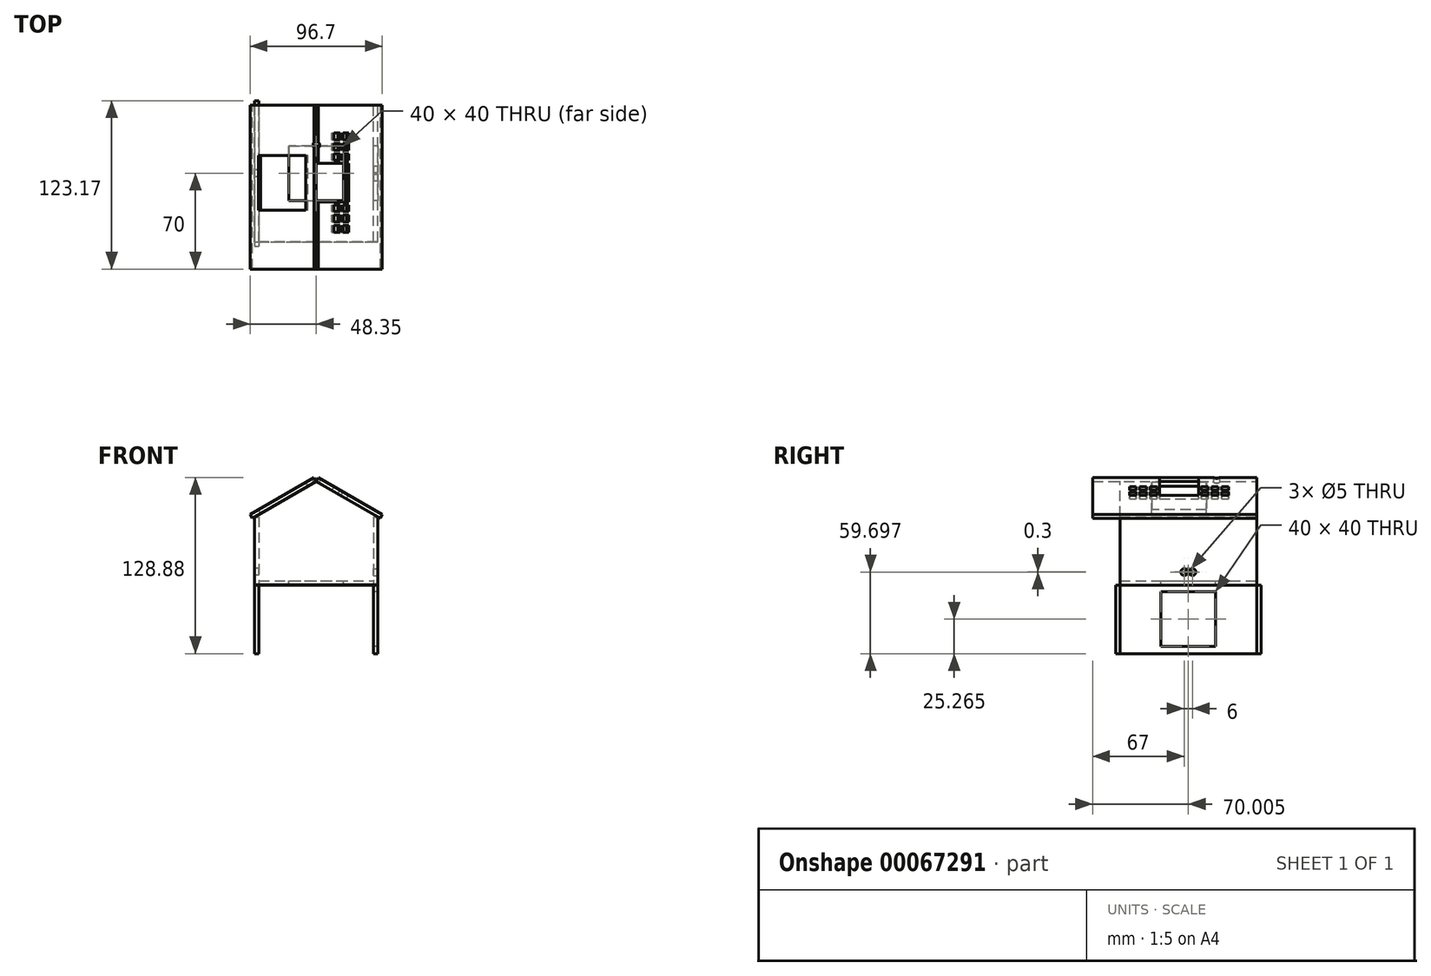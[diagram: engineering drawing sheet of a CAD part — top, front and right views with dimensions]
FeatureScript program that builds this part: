
annotation { "Feature Type Name" : "Feature", "Feature Type Description" : "" }
export const myFeature = defineFeature(function(context is Context, id is Id, definition is map)
    precondition{}
    {
        {
            var Q0;
            Q0=qCreatedBy(makeId("Front.planeOp"),FACE);
            var sketch = newSketch(context, id + "F0", { "sketchPlane" : qUnion([Q0])});
            skLineSegment(sketch, "E0.rect.bottom", {"start": v(-45, -25) * mm, "end": v(45, -25) * mm});
            skLineSegment(sketch, "E0.rect.top", {"start": v(-45, 25) * mm, "end": v(45, 25) * mm});
            skLineSegment(sketch, "E0.rect.left", {"start": v(-45, -25) * mm, "end": v(-45, 25) * mm});
            skLineSegment(sketch, "E0.rect.right", {"start": v(45, -25) * mm, "end": v(45, 25) * mm});
            skPoint(sketch, "E0.rect.middle", {"position": v(0, 0) * mm});
            skLineSegment(sketch, "E1", {"start": v(0, 25) * mm, "end": v(0, 50.98) * mm});
            skPoint(sketch, "E1.endSnap0", {"position": v(0, 25) * mm});
            skLineSegment(sketch, "E2", {"start": v(45, 25) * mm, "end": v(0, 50.98) * mm});
            skLineSegment(sketch, "E3", {"start": v(0, 50.98) * mm, "end": v(-45, 25) * mm});
            skSolve(sketch);
        }
        {
            var Q0;
            Q0 = qSketchRegion(id + "F0", true);
            extrude(context, id + "F1", {"entities" : qUnion([Q0]), "oppositeDirection" : true, "depth" : 1 / 203.2 * mm});
        }
        {
            var Q0;
            Q0=qCreatedBy(makeId("Front.planeOp"),FACE);
            var sketch = newSketch(context, id + "F2", { "sketchPlane" : qUnion([Q0])});
            skLineSegment(sketch, "E4.bottom", {"start": v(41.87, 24.95) * mm, "end": v(45.04, 24.95) * mm});
            skLineSegment(sketch, "E4.top", {"start": v(41.87, -25.05) * mm, "end": v(45.04, -25.05) * mm});
            skLineSegment(sketch, "E4.left", {"start": v(41.87, 24.95) * mm, "end": v(41.87, -25.05) * mm});
            skLineSegment(sketch, "E4.right", {"start": v(45.04, 24.95) * mm, "end": v(45.04, -25.05) * mm});
            skSolve(sketch);
        }
        {
            var Q0;
            Q0 = qSketchRegion(id + "F2", true);
            extrude(context, id + "F3", {"entities" : qUnion([Q0]), "depth" : 100 * mm});
        }
        {
            var Q0;
            Q0=qCreatedBy(makeId("Front.planeOp"),FACE);
            var sketch = newSketch(context, id + "F4", { "sketchPlane" : qUnion([Q0])});
            skLineSegment(sketch, "E5.bottom", {"start": v(-45, 25) * mm, "end": v(-41.83, 25) * mm});
            skLineSegment(sketch, "E5.top", {"start": v(-45, -25) * mm, "end": v(-41.83, -25) * mm});
            skLineSegment(sketch, "E5.left", {"start": v(-45, 25) * mm, "end": v(-45, -25) * mm});
            skLineSegment(sketch, "E5.right", {"start": v(-41.83, 25) * mm, "end": v(-41.83, -25) * mm});
            skSolve(sketch);
        }
        {
            var Q0;
            Q0 = qSketchRegion(id + "F4", true);
            extrude(context, id + "F5", {"entities" : qUnion([Q0]), "depth" : 100 * mm});
        }
        {
            var Q0;
            Q0=makeQuery(id+"F5.opExtrude","CAP_FACE",FACE,{"disambiguationData":[OSD([sQuery(id+"F4.wireOp",EDGE,"E5.bottom"),sQuery(id+"F4.wireOp",EDGE,"E5.top"),sQuery(id+"F4.wireOp",EDGE,"E5.left"),sQuery(id+"F4.wireOp",EDGE,"E5.right")])],"isStart":false});
            var sketch = newSketch(context, id + "F6", { "sketchPlane" : qUnion([Q0])});
            skLineSegment(sketch, "E6.rect.top", {"start": v(-45, 25.24) * mm, "end": v(45, 25.24) * mm});
            skLineSegment(sketch, "E6.rect.bottom", {"start": v(-45, -24.76) * mm, "end": v(45, -24.76) * mm});
            skLineSegment(sketch, "E6.rect.left", {"start": v(-45, -24.76) * mm, "end": v(-45, 25.24) * mm});
            skLineSegment(sketch, "E6.rect.right", {"start": v(45, -24.76) * mm, "end": v(45, 25.24) * mm});
            skLineSegment(sketch, "E7", {"start": v(0, 25.24) * mm, "end": v(0, 51.22) * mm});
            skLineSegment(sketch, "E8", {"start": v(45, 25.24) * mm, "end": v(0, 51.22) * mm});
            skLineSegment(sketch, "E9", {"start": v(0, 51.22) * mm, "end": v(-45, 25.24) * mm});
            skPoint(sketch, "E6.rect.middle", {"position": v(0, 0.24) * mm});
            skPoint(sketch, "E7.endSnap0", {"position": v(0, 25.24) * mm});
            skSolve(sketch);
        }
        {
            var Q0;
            Q0 = qSketchRegion(id + "F6", true);
            extrude(context, id + "F7", {"entities" : qUnion([Q0]), "depth" : 1 / 203.2 * mm});
        }
        {
            var Q0;
            Q0=qCreatedBy(makeId("Front.planeOp"),FACE);
            var sketch = newSketch(context, id + "F8", { "sketchPlane" : qUnion([Q0])});
            skLineSegment(sketch, "E10.bottom", {"start": v(-41.83, -21.82) * mm, "end": v(41.82, -21.82) * mm});
            skLineSegment(sketch, "E10.top", {"start": v(-41.83, -25) * mm, "end": v(41.82, -25) * mm});
            skLineSegment(sketch, "E10.left", {"start": v(-41.83, -21.82) * mm, "end": v(-41.83, -25) * mm});
            skLineSegment(sketch, "E10.right", {"start": v(41.82, -21.82) * mm, "end": v(41.82, -25) * mm});
            skSolve(sketch);
        }
        {
            var Q0;
            Q0 = qSketchRegion(id + "F8", true);
            extrude(context, id + "F9", {"entities" : qUnion([Q0]), "depth" : 100 * mm});
        }
        {
            var Q0;
            Q0=qCreatedBy(makeId("Front.planeOp"),FACE);
            var sketch = newSketch(context, id + "F10", { "sketchPlane" : qUnion([Q0])});
            skLineSegment(sketch, "E11.bottom", {"start": v(41.87, -25.05) * mm, "end": v(45.04, -25.05) * mm});
            skLineSegment(sketch, "E11.top", {"start": v(41.87, -75.05) * mm, "end": v(45.04, -75.05) * mm});
            skLineSegment(sketch, "E11.left", {"start": v(41.87, -25.05) * mm, "end": v(41.87, -75.05) * mm});
            skLineSegment(sketch, "E11.right", {"start": v(45.04, -25.05) * mm, "end": v(45.04, -75.05) * mm});
            skSolve(sketch);
        }
        {
            var Q0;
            Q0 = qSketchRegion(id + "F10", true);
            extrude(context, id + "F11", {"entities" : qUnion([Q0]), "depth" : 100 * mm + 1 / 203.2 * mm, "hasSecondDirection" : true, "secondDirectionOppositeDirection" : true, "secondDirectionDepth" : 1 / 203.2 * mm});
        }
        {
            var Q0;
            Q0=qCreatedBy(makeId("Top.planeOp"),FACE);
            var sketch = newSketch(context, id + "F12", { "sketchPlane" : qUnion([Q0])});
            skLineSegment(sketch, "E12.rect.bottom", {"start": v(-20, -70) * mm, "end": v(20, -70) * mm});
            skLineSegment(sketch, "E12.rect.top", {"start": v(-20, -30) * mm, "end": v(20, -30) * mm});
            skLineSegment(sketch, "E12.rect.left", {"start": v(-20, -70) * mm, "end": v(-20, -30) * mm});
            skLineSegment(sketch, "E12.rect.right", {"start": v(20, -70) * mm, "end": v(20, -30) * mm});
            skPoint(sketch, "E12.rect.middle", {"position": v(0, -50) * mm});
            skSolve(sketch);
        }
        {
            var Q0;
            Q0 = qSketchRegion(id + "F12", true);
            var Q1;
            Q1=makeQuery(id+"F9.opExtrude","SWEPT_FACE",FACE,{"disambiguationData":[OSD([sQuery(id+"F8.wireOp",EDGE,"E10.top")])]});
            extrude(context, id + "F13", {"entities" : qUnion([Q0]), "operationType" : NewBodyOperationType.REMOVE, "endBound" : BoundingType.UP_TO_SURFACE, "oppositeDirection" : true, "endBoundEntityFace" : qUnion([Q1]), "depth" : 25 * mm});
        }
        {
            var Q0;
            Q0=makeQuery(id+"F1.opExtrude","CAP_FACE",FACE,{"disambiguationData":[OSD([sQuery(id+"F0.wireOp",EDGE,"E0.rect.bottom"),sQuery(id+"F0.wireOp",EDGE,"E0.rect.left"),sQuery(id+"F0.wireOp",EDGE,"E0.rect.right"),sQuery(id+"F0.wireOp",EDGE,"E2"),sQuery(id+"F0.wireOp",EDGE,"E3")])],"isStart":false});
            var sketch = newSketch(context, id + "F14", { "sketchPlane" : qUnion([Q0])});
            skLineSegment(sketch, "E13", {"start": v(0, 51.08) * mm, "end": v(46.77, 24.08) * mm});
            skLineSegment(sketch, "E14", {"start": v(1.59, 53.83) * mm, "end": v(0, 51.08) * mm});
            skLineSegment(sketch, "E15", {"start": v(48.35, 26.83) * mm, "end": v(46.77, 24.08) * mm});
            skLineSegment(sketch, "E16", {"start": v(48.35, 26.83) * mm, "end": v(1.59, 53.83) * mm});
            skSolve(sketch);
        }
        {
            var Q0;
            {var subQ1=sQuery(id+"F14.wireOp",EDGE,"E14");Q0=makeQuery(id+"F14.imprint","IMPRINT",FACE,{"disambiguationData":[TD([[makeQuery(id+"F14.imprint","IMPRINT",EDGE,{"derivedFrom":subQ1}),1.0]])]});}
            extrude(context, id + "F15", {"entities" : qUnion([Q0]), "oppositeDirection" : true, "depth" : 120 * mm});
        }
        {
            var Q0;
            Q0=makeQuery(id+"F15.opExtrude","SWEPT_FACE",FACE,{"disambiguationData":[OSD([sQuery(id+"F14.wireOp",EDGE,"E13")])]});
            var sketch = newSketch(context, id + "F16", { "sketchPlane" : qUnion([Q0])});
            skSolve(sketch);
        }
        {
            var Q0;
            Q0=makeQuery(id+"F1.opExtrude","CAP_FACE",FACE,{"disambiguationData":[OSD([sQuery(id+"F0.wireOp",EDGE,"E0.rect.bottom"),sQuery(id+"F0.wireOp",EDGE,"E0.rect.left"),sQuery(id+"F0.wireOp",EDGE,"E0.rect.right"),sQuery(id+"F0.wireOp",EDGE,"E2"),sQuery(id+"F0.wireOp",EDGE,"E3")])],"isStart":false});
            var sketch = newSketch(context, id + "F17", { "sketchPlane" : qUnion([Q0])});
            skLineSegment(sketch, "E17", {"start": v(-46.77, 23.98) * mm, "end": v(0, 50.98) * mm});
            skLineSegment(sketch, "E18", {"start": v(-1.59, 53.73) * mm, "end": v(-48.35, 26.73) * mm});
            skLineSegment(sketch, "E19", {"start": v(-48.35, 26.73) * mm, "end": v(-46.77, 23.98) * mm});
            skLineSegment(sketch, "E20", {"start": v(-1.59, 53.73) * mm, "end": v(0, 50.98) * mm});
            skSolve(sketch);
        }
        {
            var Q0;
            Q0=makeQuery(id+"F17.imprint","IMPRINT",FACE,{"disambiguationData":[TD([[makeQuery(id+"F17.imprint","IMPRINT",EDGE,{"derivedFrom":sQuery(id+"F17.wireOp",EDGE,"E18")}),1.0]])]});
            extrude(context, id + "F18", {"entities" : qUnion([Q0]), "oppositeDirection" : true, "depth" : 120 * mm});
        }
        {
            var Q0;
            Q0=makeQuery(id+"F15.opExtrude","SWEPT_FACE",FACE,{"disambiguationData":[OSD([sQuery(id+"F14.wireOp",EDGE,"E16")])]});
            var sketch = newSketch(context, id + "F19", { "sketchPlane" : qUnion([Q0])});
            skLineSegment(sketch, "E21.bottom", {"start": v(18.54, -36.83) * mm, "end": v(-21.46, -36.83) * mm});
            skLineSegment(sketch, "E21.top", {"start": v(18.54, -76.83) * mm, "end": v(-21.46, -76.83) * mm});
            skLineSegment(sketch, "E21.left", {"start": v(18.54, -36.83) * mm, "end": v(18.54, -76.83) * mm});
            skLineSegment(sketch, "E21.right", {"start": v(-21.46, -36.83) * mm, "end": v(-21.46, -76.83) * mm});
            skSolve(sketch);
        }
        {
            var Q0;
            Q0 = qSketchRegion(id + "F19", true);
            extrude(context, id + "F20", {"entities" : qUnion([Q0]), "operationType" : NewBodyOperationType.REMOVE, "oppositeDirection" : true, "depth" : 25 * mm});
        }
        {
            var Q0;
            Q0=makeQuery(id+"F3.opExtrude","SWEPT_FACE",FACE,{"disambiguationData":[OSD([sQuery(id+"F2.wireOp",EDGE,"E4.right")])]});
            var sketch = newSketch(context, id + "F21", { "sketchPlane" : qUnion([Q0])});
            skCircle(sketch, "E22", {"center": v(-53, -15.35) * mm, "radius": 2.5 * mm});
            skCircle(sketch, "E23", {"center": v(-47, -15.35) * mm, "radius": 2.5 * mm});
            skLineSegment(sketch, "E24", {"start": v(-50, -6.63) * mm, "end": v(-50, -21.83) * mm, "construction": true});
            skSolve(sketch);
        }
        {
            var Q0;
            Q0 = qSketchRegion(id + "F21", true);
            var Q1;
            Q1=makeQuery(id+"F3.opExtrude","SWEPT_BODY",BODY,{"disambiguationData":[OSD([sQuery(id+"F2.wireOp",EDGE,"E4.bottom"),sQuery(id+"F2.wireOp",EDGE,"E4.top"),sQuery(id+"F2.wireOp",EDGE,"E4.left"),sQuery(id+"F2.wireOp",EDGE,"E4.right")])]});
            extrude(context, id + "F22", {"entities" : qUnion([Q0]), "operationType" : NewBodyOperationType.REMOVE, "endBound" : BoundingType.UP_TO_NEXT, "oppositeDirection" : true, "endBoundEntityBody" : qUnion([Q1]), "depth" : 25 * mm});
        }
        {
            var Q0;
            Q0=makeQuery(id+"F18.opExtrude","SWEPT_FACE",FACE,{"disambiguationData":[OSD([sQuery(id+"F17.wireOp",EDGE,"E18")])]});
            var sketch = newSketch(context, id + "F23", { "sketchPlane" : qUnion([Q0])});
            skLineSegment(sketch, "E25", {"start": v(-25.5, -56.83) * mm, "end": v(28.5, -56.83) * mm, "construction": true});
            skLineSegment(sketch, "E26.left", {"start": v(-12.24, -93.08) * mm, "end": v(-12.24, -88.08) * mm});
            skLineSegment(sketch, "E26.right", {"start": v(-7.24, -93.08) * mm, "end": v(-7.24, -88.08) * mm});
            skLineSegment(sketch, "E26.top", {"start": v(-12.24, -88.07) * mm, "end": v(-7.24, -88.07) * mm});
            skLineSegment(sketch, "E26.bottom", {"start": v(-12.24, -93.07) * mm, "end": v(-7.24, -93.07) * mm});
            skLineSegment(sketch, "E27.0.1.0", {"start": v(-12.24, -85.58) * mm, "end": v(-12.24, -80.58) * mm});
            skLineSegment(sketch, "E27.0.1.1", {"start": v(-12.24, -85.58) * mm, "end": v(-7.24, -85.58) * mm});
            skLineSegment(sketch, "E27.0.1.2", {"start": v(-12.24, -80.58) * mm, "end": v(-7.24, -80.58) * mm});
            skLineSegment(sketch, "E27.0.1.3", {"start": v(-7.24, -85.58) * mm, "end": v(-7.24, -80.58) * mm});
            skLineSegment(sketch, "E27.0.2.0", {"start": v(-12.24, -78.08) * mm, "end": v(-12.24, -73.08) * mm});
            skLineSegment(sketch, "E27.0.2.1", {"start": v(-12.24, -78.08) * mm, "end": v(-7.24, -78.08) * mm});
            skLineSegment(sketch, "E27.0.2.2", {"start": v(-12.24, -73.08) * mm, "end": v(-7.24, -73.08) * mm});
            skLineSegment(sketch, "E27.0.2.3", {"start": v(-7.24, -78.08) * mm, "end": v(-7.24, -73.08) * mm});
            skLineSegment(sketch, "E27.0.7.0", {"start": v(-12.24, -40.58) * mm, "end": v(-12.24, -35.58) * mm});
            skLineSegment(sketch, "E27.0.7.1", {"start": v(-12.24, -40.58) * mm, "end": v(-7.24, -40.58) * mm});
            skLineSegment(sketch, "E27.0.7.2", {"start": v(-12.24, -35.58) * mm, "end": v(-7.24, -35.58) * mm});
            skLineSegment(sketch, "E27.0.7.3", {"start": v(-7.24, -40.58) * mm, "end": v(-7.24, -35.58) * mm});
            skLineSegment(sketch, "E27.0.8.0", {"start": v(-12.24, -33.08) * mm, "end": v(-12.24, -28.08) * mm});
            skLineSegment(sketch, "E27.0.8.1", {"start": v(-12.24, -33.08) * mm, "end": v(-7.24, -33.08) * mm});
            skLineSegment(sketch, "E27.0.8.2", {"start": v(-12.24, -28.08) * mm, "end": v(-7.24, -28.08) * mm});
            skLineSegment(sketch, "E27.0.8.3", {"start": v(-7.24, -33.08) * mm, "end": v(-7.24, -28.08) * mm});
            skLineSegment(sketch, "E27.0.9.0", {"start": v(-12.24, -25.58) * mm, "end": v(-12.24, -20.58) * mm});
            skLineSegment(sketch, "E27.0.9.1", {"start": v(-12.24, -25.58) * mm, "end": v(-7.24, -25.58) * mm});
            skLineSegment(sketch, "E27.0.9.2", {"start": v(-12.24, -20.58) * mm, "end": v(-7.24, -20.58) * mm});
            skLineSegment(sketch, "E27.0.9.3", {"start": v(-7.24, -25.58) * mm, "end": v(-7.24, -20.58) * mm});
            skLineSegment(sketch, "E27.1.0.0", {"start": v(-4.74, -93.08) * mm, "end": v(-4.74, -88.08) * mm});
            skLineSegment(sketch, "E27.1.0.1", {"start": v(-4.74, -93.07) * mm, "end": v(0.26, -93.07) * mm});
            skLineSegment(sketch, "E27.1.0.2", {"start": v(-4.74, -88.07) * mm, "end": v(0.26, -88.07) * mm});
            skLineSegment(sketch, "E27.1.0.3", {"start": v(0.26, -93.08) * mm, "end": v(0.26, -88.08) * mm});
            skLineSegment(sketch, "E27.1.1.0", {"start": v(-4.74, -85.58) * mm, "end": v(-4.74, -80.58) * mm});
            skLineSegment(sketch, "E27.1.1.1", {"start": v(-4.74, -85.58) * mm, "end": v(0.26, -85.58) * mm});
            skLineSegment(sketch, "E27.1.1.2", {"start": v(-4.74, -80.58) * mm, "end": v(0.26, -80.58) * mm});
            skLineSegment(sketch, "E27.1.1.3", {"start": v(0.26, -85.58) * mm, "end": v(0.26, -80.58) * mm});
            skLineSegment(sketch, "E27.1.2.0", {"start": v(-4.74, -78.08) * mm, "end": v(-4.74, -73.08) * mm});
            skLineSegment(sketch, "E27.1.2.1", {"start": v(-4.74, -78.08) * mm, "end": v(0.26, -78.08) * mm});
            skLineSegment(sketch, "E27.1.2.2", {"start": v(-4.74, -73.08) * mm, "end": v(0.26, -73.08) * mm});
            skLineSegment(sketch, "E27.1.2.3", {"start": v(0.26, -78.08) * mm, "end": v(0.26, -73.08) * mm});
            skLineSegment(sketch, "E27.1.7.0", {"start": v(-4.74, -40.58) * mm, "end": v(-4.74, -35.58) * mm});
            skLineSegment(sketch, "E27.1.7.1", {"start": v(-4.74, -40.58) * mm, "end": v(0.26, -40.58) * mm});
            skLineSegment(sketch, "E27.1.7.2", {"start": v(-4.74, -35.58) * mm, "end": v(0.26, -35.58) * mm});
            skLineSegment(sketch, "E27.1.7.3", {"start": v(0.26, -40.58) * mm, "end": v(0.26, -35.58) * mm});
            skLineSegment(sketch, "E27.1.8.0", {"start": v(-4.74, -33.08) * mm, "end": v(-4.74, -28.08) * mm});
            skLineSegment(sketch, "E27.1.8.1", {"start": v(-4.74, -33.08) * mm, "end": v(0.26, -33.08) * mm});
            skLineSegment(sketch, "E27.1.8.2", {"start": v(-4.74, -28.08) * mm, "end": v(0.26, -28.08) * mm});
            skLineSegment(sketch, "E27.1.8.3", {"start": v(0.26, -33.08) * mm, "end": v(0.26, -28.08) * mm});
            skLineSegment(sketch, "E27.1.9.0", {"start": v(-4.74, -25.58) * mm, "end": v(-4.74, -20.58) * mm});
            skLineSegment(sketch, "E27.1.9.1", {"start": v(-4.74, -25.58) * mm, "end": v(0.26, -25.58) * mm});
            skLineSegment(sketch, "E27.1.9.2", {"start": v(-4.74, -20.58) * mm, "end": v(0.26, -20.58) * mm});
            skLineSegment(sketch, "E27.1.9.3", {"start": v(0.26, -25.58) * mm, "end": v(0.26, -20.58) * mm});
            skLineSegment(sketch, "E27.direction1", {"start": v(-12.24, -93.07) * mm, "end": v(-4.74, -93.07) * mm, "construction": true});
            skLineSegment(sketch, "E27.direction2", {"start": v(-12.24, -93.08) * mm, "end": v(-12.24, -85.58) * mm, "construction": true});
            skLineSegment(sketch, "E28.bottom", {"start": v(-25.5, -71.08) * mm, "end": v(0.26, -71.08) * mm});
            skLineSegment(sketch, "E28.top", {"start": v(-25.5, -42.58) * mm, "end": v(0.26, -42.58) * mm});
            skLineSegment(sketch, "E28.left", {"start": v(-25.5, -71.08) * mm, "end": v(-25.5, -42.58) * mm});
            skLineSegment(sketch, "E28.right", {"start": v(0.26, -71.08) * mm, "end": v(0.26, -42.58) * mm});
            skSolve(sketch);
        }
        {
            var Q0;
            Q0 = qSketchRegion(id + "F23", true);
            var Q1;
            Q1=makeQuery(id+"F18.opExtrude","SWEPT_BODY",BODY,{"disambiguationData":[OSD([sQuery(id+"F17.wireOp",EDGE,"E17"),sQuery(id+"F17.wireOp",EDGE,"E18"),sQuery(id+"F17.wireOp",EDGE,"E19"),sQuery(id+"F17.wireOp",EDGE,"E20")])]});
            extrude(context, id + "F24", {"entities" : qUnion([Q0]), "operationType" : NewBodyOperationType.REMOVE, "endBound" : BoundingType.UP_TO_BODY, "oppositeDirection" : true, "endBoundEntityBody" : qUnion([Q1]), "depth" : 1 / 203.2 * mm});
        }
        {
            var Q0;
            Q0=qCreatedBy(makeId("Top.planeOp"),FACE);
            var sketch = newSketch(context, id + "F25", { "sketchPlane" : qUnion([Q0])});
            skCircle(sketch, "E29", {"center": v(0.03, -29.33) * mm, "radius": 2.5 * mm});
            skSolve(sketch);
        }
        {
            var Q0;
            Q0=makeQuery(id+"F25.imprint","IMPRINT",FACE,{"disambiguationData":[TD([[makeQuery(id+"F25.imprint","IMPRINT",EDGE,{"derivedFrom":sQuery(id+"F25.wireOp",EDGE,"E29")}),1.0]])]});
            extrude(context, id + "F26", {"entities" : qUnion([Q0]), "operationType" : NewBodyOperationType.REMOVE, "endBound" : BoundingType.THROUGH_ALL, "depth" : 25 * mm});
        }
        {
            var Q0;
            Q0=makeQuery(id+"F11.opExtrude","SWEPT_FACE",FACE,{"disambiguationData":[OSD([sQuery(id+"F10.wireOp",EDGE,"E11.left")])]});
            var sketch = newSketch(context, id + "F27", { "sketchPlane" : qUnion([Q0])});
            skLineSegment(sketch, "E30.bottom", {"start": v(70, -29.78) * mm, "end": v(30, -29.78) * mm});
            skLineSegment(sketch, "E30.top", {"start": v(70, -69.78) * mm, "end": v(30, -69.78) * mm});
            skLineSegment(sketch, "E30.left", {"start": v(70, -29.78) * mm, "end": v(70, -69.78) * mm});
            skLineSegment(sketch, "E30.right", {"start": v(30, -29.78) * mm, "end": v(30, -69.78) * mm});
            skSolve(sketch);
        }
        {
            var Q0;
            Q0 = qSketchRegion(id + "F27", true);
            extrude(context, id + "F28", {"entities" : qUnion([Q0]), "operationType" : NewBodyOperationType.REMOVE, "oppositeDirection" : true, "depth" : 25 * mm});
        }
        {
            var Q0;
            Q0=makeQuery(id+"F1.opExtrude","SWEPT_FACE",FACE,{"disambiguationData":[OSD([sQuery(id+"F0.wireOp",EDGE,"E0.rect.bottom")])]});
            var sketch = newSketch(context, id + "F29", { "sketchPlane" : qUnion([Q0])});
            skLineSegment(sketch, "E31.bottom", {"start": v(-45, -3.18) * mm, "end": v(-41.82, -3.18) * mm});
            skLineSegment(sketch, "E31.top", {"start": v(-45, 103.17) * mm, "end": v(-41.83, 103.17) * mm});
            skLineSegment(sketch, "E31.left", {"start": v(-45, -3.17) * mm, "end": v(-45, 103.17) * mm});
            skLineSegment(sketch, "E31.right", {"start": v(-41.82, -3.17) * mm, "end": v(-41.82, 103.17) * mm});
            skSolve(sketch);
        }
        {
            var Q0;
            Q0 = qSketchRegion(id + "F29", true);
            extrude(context, id + "F30", {"entities" : qUnion([Q0]), "depth" : 50 * mm});
        }
        {
            var Q0;
            Q0=makeQuery(id+"F5.opExtrude","SWEPT_FACE",FACE,{"disambiguationData":[OSD([sQuery(id+"F4.wireOp",EDGE,"E5.left")])]});
            var sketch = newSketch(context, id + "F31", { "sketchPlane" : qUnion([Q0])});
            skCircle(sketch, "E32", {"center": v(50, -15.05) * mm, "radius": 2.5 * mm});
            skSolve(sketch);
        }
        {
            var Q0;
            Q0 = qSketchRegion(id + "F31", true);
            extrude(context, id + "F32", {"entities" : qUnion([Q0]), "operationType" : NewBodyOperationType.REMOVE, "oppositeDirection" : true, "depth" : 25 * mm});
        }
    });
